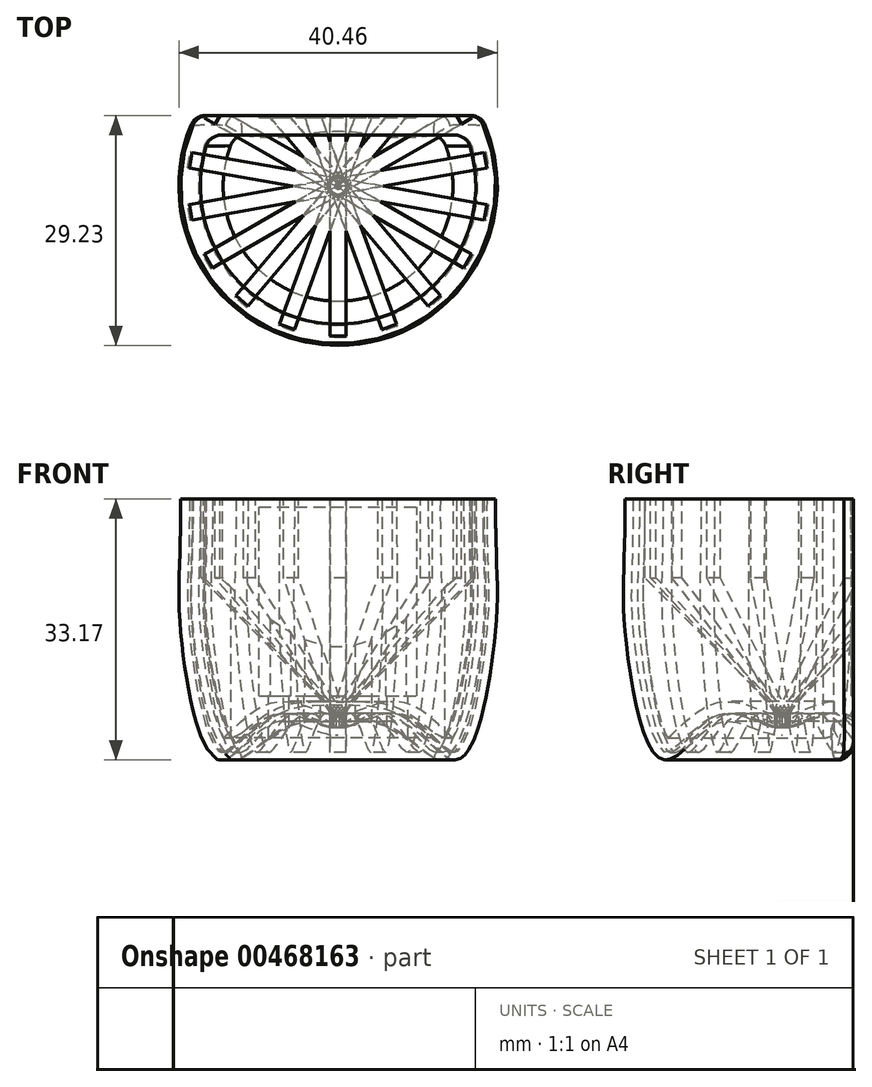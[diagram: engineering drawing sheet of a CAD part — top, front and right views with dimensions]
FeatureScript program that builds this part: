
annotation { "Feature Type Name" : "Feature", "Feature Type Description" : "" }
export const myFeature = defineFeature(function(context is Context, id is Id, definition is map)
    precondition{}
    {
        {
            var Q0;
            Q0=qCreatedBy(makeId("Right.planeOp"),FACE);
            var sketch = newSketch(context, id + "F0", { "sketchPlane" : qUnion([Q0])});
            skLineSegment(sketch, "E0", {"start": v(-9, 0) * mm, "end": v(-9, 30) * mm});
            skLineSegment(sketch, "E1", {"start": v(-9, 30) * mm, "end": v(-29, 30) * mm});
            skLineSegment(sketch, "E2", {"start": v(-29, 30) * mm, "end": v(-30, 30) * mm});
            skLineSegment(sketch, "E3", {"start": v(-30, 30) * mm, "end": v(-30, 26) * mm});
            skFitSpline(sketch, "E4", {"points": [v(-29, 30) * mm, v(-29, 13.26) * mm, v(-24.15, -3.15) * mm, v(-17.1, 1.58) * mm, v(-9, 0) * mm], "startDerivative": vector(0, -98.3) * mm, "endDerivative": vector(45.2, 0) * mm});
            skLineSegment(sketch, "E5", {"start": v(-9, 2.5) * mm, "end": v(-26.5, 20) * mm});
            skLineSegment(sketch, "E6", {"start": v(-30, 26) * mm, "end": v(-29.03, 26) * mm});
            skLineSegment(sketch, "E7", {"start": v(-26.5, 20) * mm, "end": v(-26.5, 30) * mm});
            skFitSpline(sketch, "E8.0", {"points": [v(-28, 30) * mm, v(-28, 27.94) * mm, v(-28.05, 24.57) * mm, v(-28.17, 21.03) * mm, v(-28.23, 18.75) * mm, v(-28.22, 16.98) * mm, v(-28.17, 15.57) * mm, v(-28.08, 14.26) * mm, v(-27.98, 13.08) * mm, v(-27.85, 11.8) * mm, v(-27.65, 10.06) * mm, v(-27.34, 7.85) * mm, v(-26.95, 5.62) * mm, v(-26.5, 3.46) * mm, v(-25.97, 1.5) * mm, v(-25.47, 0.1) * mm, v(-25.06, -0.82) * mm, v(-24.75, -1.38) * mm, v(-24.44, -1.8) * mm, v(-24.18, -2.06) * mm, v(-24.02, -2.15) * mm, v(-23.95, -2.17) * mm, v(-23.89, -2.18) * mm, v(-23.76, -2.17) * mm, v(-23.47, -2.07) * mm, v(-23.1, -1.86) * mm, v(-22.66, -1.53) * mm, v(-22.17, -1.13) * mm, v(-21.49, -0.5) * mm, v(-20.57, 0.38) * mm, v(-19.58, 1.26) * mm, v(-18.74, 1.88) * mm, v(-18.18, 2.2) * mm, v(-17.71, 2.43) * mm, v(-17.22, 2.6) * mm, v(-16.6, 2.75) * mm, v(-15.86, 2.78) * mm, v(-14.92, 2.7) * mm, v(-13.81, 2.4) * mm, v(-12.56, 1.91) * mm, v(-11.35, 1.44) * mm, v(-10.17, 1.1) * mm, v(-9.4, 1) * mm, v(-9, 1) * mm]});
            skSolve(sketch);
        }
        {
            var Q0;
            {var subQ7=sQuery(id+"F0.wireOp",EDGE,"E5");Q0=makeQuery(id+"F0.imprint","IMPRINT",FACE,{"disambiguationData":[TD([[makeQuery(id+"F0.imprint","IMPRINT",EDGE,{"derivedFrom":subQ7}),1.0]])]});}
            var Q1;
            {var subQ3=sQuery(id+"F0.wireOp",EDGE,"E5");Q1=makeQuery(id+"F0.imprint","IMPRINT",FACE,{"disambiguationData":[TD([[makeQuery(id+"F0.imprint","IMPRINT",EDGE,{"derivedFrom":subQ3}),-1.0]])]});}
            var Q2;
            {var subQ6=sQuery(id+"F0.wireOp",EDGE,"E8.0");Q2=makeQuery(id+"F0.imprint","IMPRINT",FACE,{"disambiguationData":[TD([[makeQuery(id+"F0.imprint","IMPRINT",EDGE,{"derivedFrom":subQ6}),-1.0]])]});}
            var Q3;
            Q3=sQuery(id+"F0.wireOp",EDGE,"E0");
            revolve(context, id + "F1", {"entities" : qUnion([Q0, Q1, Q2]), "axis" : qUnion([Q3]), "revolveType" : RevolveType.FULL});
        }
        {
            var Q0;
            Q0=qCreatedBy(makeId("Front.planeOp"),FACE);
            var sketch = newSketch(context, id + "F2", { "sketchPlane" : qUnion([Q0])});
            skLineSegment(sketch, "E9.bottom", {"start": v(50, 50) * mm, "end": v(-50, 50) * mm});
            skLineSegment(sketch, "E9.top", {"start": v(50, -50) * mm, "end": v(-50, -50) * mm});
            skLineSegment(sketch, "E9.left", {"start": v(50, 50) * mm, "end": v(50, -50) * mm});
            skLineSegment(sketch, "E9.right", {"start": v(-50, 50) * mm, "end": v(-50, -50) * mm});
            skPoint(sketch, "E9.middle", {"position": v(0, 0) * mm});
            skSolve(sketch);
        }
        {
            var Q0;
            Q0=makeQuery(id+"F2.imprint","IMPRINT",FACE,{"disambiguationData":[TD([[makeQuery(id+"F2.imprint","IMPRINT",EDGE,{"derivedFrom":sQuery(id+"F2.wireOp",EDGE,"E9.bottom")}),1.0]])]});
            extrude(context, id + "F3", {"entities" : qUnion([Q0]), "operationType" : NewBodyOperationType.REMOVE, "oppositeDirection" : true, "depth" : 25 * mm});
        }
        {
            var Q0;
            Q0=makeQuery(id+"F1.opRevolve","SWEPT_FACE",FACE,{"disambiguationData":[OSD([sQuery(id+"F0.wireOp",EDGE,"E1")])]});
            shell(context, id + "F4", {"entities" : qUnion([Q0]), "thickness" : 2.5 * mm});
        }
        {
            var Q0;
            {var subQ1=sQuery(id+"F0.wireOp",EDGE,"E5");Q0=makeQuery(id+"F0.imprint","IMPRINT",FACE,{"disambiguationData":[TD([[makeQuery(id+"F0.imprint","IMPRINT",EDGE,{"derivedFrom":subQ1}),1.0]])]});}
            extrude(context, id + "F5", {"entities" : qUnion([Q0]), "endBound" : BoundingType.SYMMETRIC, "depth" : 2 * mm});
        }
        {
            var Q0;
            Q0=makeQuery(id+"F5.opExtrude","SWEPT_BODY",BODY,{"disambiguationData":[OSD([sQuery(id+"F0.wireOp",EDGE,"E0"),sQuery(id+"F0.wireOp",EDGE,"E1"),sQuery(id+"F0.wireOp",EDGE,"E5"),sQuery(id+"F0.wireOp",EDGE,"E7"),sQuery(id+"F0.wireOp",EDGE,"E8.0")])]});
            var Q1;
            Q1=sQuery(id+"F0.wireOp",EDGE,"E0");
            circularPattern(context, id + "F6", {"entities" : qUnion([Q0]), "axis" : qUnion([Q1]), "angle" : 360 * degree, "instanceCount" : 18, "equalSpace" : true});
        }
        {
            var Q0;
            Q0=makeQuery(id+"F2.imprint","IMPRINT",FACE,{"disambiguationData":[TD([[makeQuery(id+"F2.imprint","IMPRINT",EDGE,{"derivedFrom":sQuery(id+"F2.wireOp",EDGE,"E9.bottom")}),1.0]])]});
            extrude(context, id + "F7", {"entities" : qUnion([Q0]), "operationType" : NewBodyOperationType.REMOVE, "oppositeDirection" : true, "depth" : 25 * mm});
        }
        {
            var Q0;
            Q0=makeQuery(id+"F3.boolean.opBoolean","COPY",FACE,{"derivedFrom":makeQuery(id+"F3.opExtrude","CAP_FACE",FACE,{"disambiguationData":[OSD([sQuery(id+"F2.wireOp",EDGE,"E9.bottom"),sQuery(id+"F2.wireOp",EDGE,"E9.top"),sQuery(id+"F2.wireOp",EDGE,"E9.left"),sQuery(id+"F2.wireOp",EDGE,"E9.right")])],"isStart":true})});
            var sketch = newSketch(context, id + "F8", { "sketchPlane" : qUnion([Q0])});
            skLineSegment(sketch, "E10.bottom", {"start": v(10.03, 5) * mm, "end": v(-10.02, 5) * mm});
            skLineSegment(sketch, "E10.top", {"start": v(10.02, 29) * mm, "end": v(-10.03, 29) * mm});
            skLineSegment(sketch, "E10.left", {"start": v(10.03, 5) * mm, "end": v(10.03, 29) * mm});
            skLineSegment(sketch, "E10.right", {"start": v(-10.02, 5) * mm, "end": v(-10.03, 29) * mm});
            skPoint(sketch, "E10.middle", {"position": v(0, 17) * mm});
            skSolve(sketch);
        }
        {
            var Q0;
            Q0=makeQuery(id+"F4.opShell","OFFSET_EDGE",EDGE,{"disambiguationData":[OSD([sQuery(id+"F0.wireOp",EDGE,"E4"),sQuery(id+"F2.wireOp",EDGE,"E9.bottom"),sQuery(id+"F2.wireOp",EDGE,"E9.top"),sQuery(id+"F2.wireOp",EDGE,"E9.left"),sQuery(id+"F2.wireOp",EDGE,"E9.right")]),OD(0.0)]});
            var Q1;
            Q1=makeQuery(id+"F4.opShell","OFFSET_EDGE",EDGE,{"disambiguationData":[OSD([sQuery(id+"F0.wireOp",EDGE,"E4"),sQuery(id+"F2.wireOp",EDGE,"E9.bottom"),sQuery(id+"F2.wireOp",EDGE,"E9.top"),sQuery(id+"F2.wireOp",EDGE,"E9.left"),sQuery(id+"F2.wireOp",EDGE,"E9.right")]),OD(1.0)]});
            var Q2;
            Q2=makeQuery(id+"F3.boolean.opBoolean","INTERSECT",EDGE,{"derivedFrom":[makeQuery(id+"F1.opRevolve","SWEPT_FACE",FACE,{"disambiguationData":[OSD([sQuery(id+"F0.wireOp",EDGE,"E4")])]}),makeQuery(id+"F3.opExtrude","CAP_FACE",FACE,{"disambiguationData":[OSD([sQuery(id+"F2.wireOp",EDGE,"E9.bottom"),sQuery(id+"F2.wireOp",EDGE,"E9.top"),sQuery(id+"F2.wireOp",EDGE,"E9.left"),sQuery(id+"F2.wireOp",EDGE,"E9.right")])],"isStart":true})]});
            fillet(context, id + "F9", {"entities" : qUnion([Q0, Q1, Q2]), "radius" : 2 * mm, "tangentPropagation" : true, "allowEdgeOverflow" : false});
        }
        {
            var Q0;
            Q0=makeQuery(id+"F8.imprint","IMPRINT",FACE,{"disambiguationData":[TD([[makeQuery(id+"F8.imprint","IMPRINT",EDGE,{"derivedFrom":sQuery(id+"F8.wireOp",EDGE,"E10.bottom")}),-1.0]])]});
            extrude(context, id + "F10", {"entities" : qUnion([Q0]), "operationType" : NewBodyOperationType.REMOVE, "oppositeDirection" : true, "depth" : .25 * mm, "offsetDistance" : 25 * mm});
        }
    });
